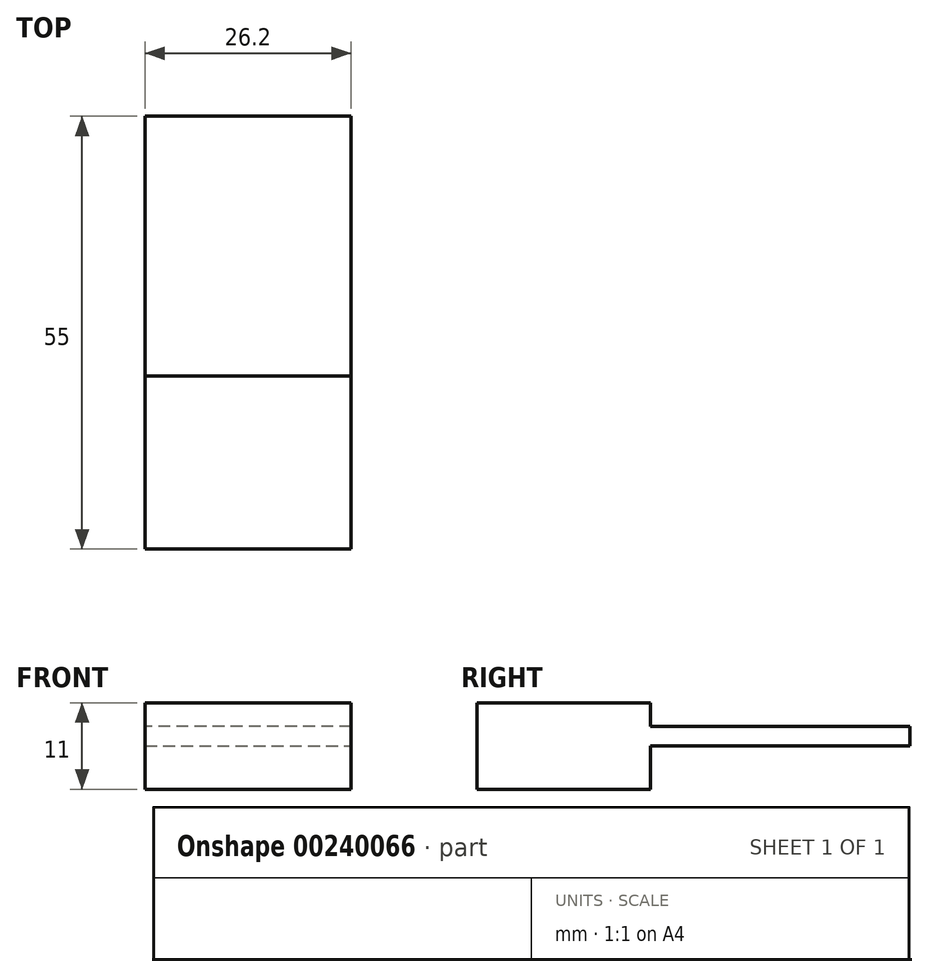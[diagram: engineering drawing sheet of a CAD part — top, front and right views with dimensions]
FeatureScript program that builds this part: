
annotation { "Feature Type Name" : "Feature", "Feature Type Description" : "" }
export const myFeature = defineFeature(function(context is Context, id is Id, definition is map)
    precondition{}
    {
        {
            var Q0;
            Q0=qCreatedBy(makeId("Top.planeOp"),FACE);
            var sketch = newSketch(context, id + "F0", { "sketchPlane" : qUnion([Q0])});
            skLineSegment(sketch, "E0.bottom", {"start": v(13.1, 27.5) * mm, "end": v(-13.1, 27.5) * mm});
            skLineSegment(sketch, "E0.top", {"start": v(13.1, -27.5) * mm, "end": v(-13.1, -27.5) * mm});
            skLineSegment(sketch, "E0.left", {"start": v(13.1, 27.5) * mm, "end": v(13.1, -27.5) * mm});
            skLineSegment(sketch, "E0.right", {"start": v(-13.1, 27.5) * mm, "end": v(-13.1, -27.5) * mm});
            skPoint(sketch, "E0.middle", {"position": v(0, 0) * mm});
            skLineSegment(sketch, "E1", {"start": v(-13.1, -5.5) * mm, "end": v(13.1, -5.5) * mm});
            skSolve(sketch);
        }
        {
            var Q0;
            {var subQ0=sQuery(id+"F0.wireOp",EDGE,"E0.bottom");Q0=makeQuery(id+"F0.imprint","IMPRINT",FACE,{"disambiguationData":[TD([[makeQuery(id+"F0.imprint","IMPRINT",EDGE,{"derivedFrom":subQ0}),1.0]])]});}
            extrude(context, id + "F1", {"entities" : qUnion([Q0]), "depth" : 2.5 * mm});
        }
        {
            var Q0;
            {var subQ0=sQuery(id+"F0.wireOp",EDGE,"E0.top");Q0=makeQuery(id+"F0.imprint","IMPRINT",FACE,{"disambiguationData":[TD([[makeQuery(id+"F0.imprint","IMPRINT",EDGE,{"derivedFrom":subQ0}),-1.0]])]});}
            extrude(context, id + "F2", {"entities" : qUnion([Q0]), "operationType" : NewBodyOperationType.ADD, "depth" : 5.5 * mm});
        }
        {
            var Q0;
            {var subQ0=sQuery(id+"F0.wireOp",EDGE,"E0.top");Q0=makeQuery(id+"F0.imprint","IMPRINT",FACE,{"disambiguationData":[TD([[makeQuery(id+"F0.imprint","IMPRINT",EDGE,{"derivedFrom":subQ0}),-1.0]])]});}
            extrude(context, id + "F3", {"entities" : qUnion([Q0]), "operationType" : NewBodyOperationType.ADD, "oppositeDirection" : true, "depth" : 5.5 * mm});
        }
    });
